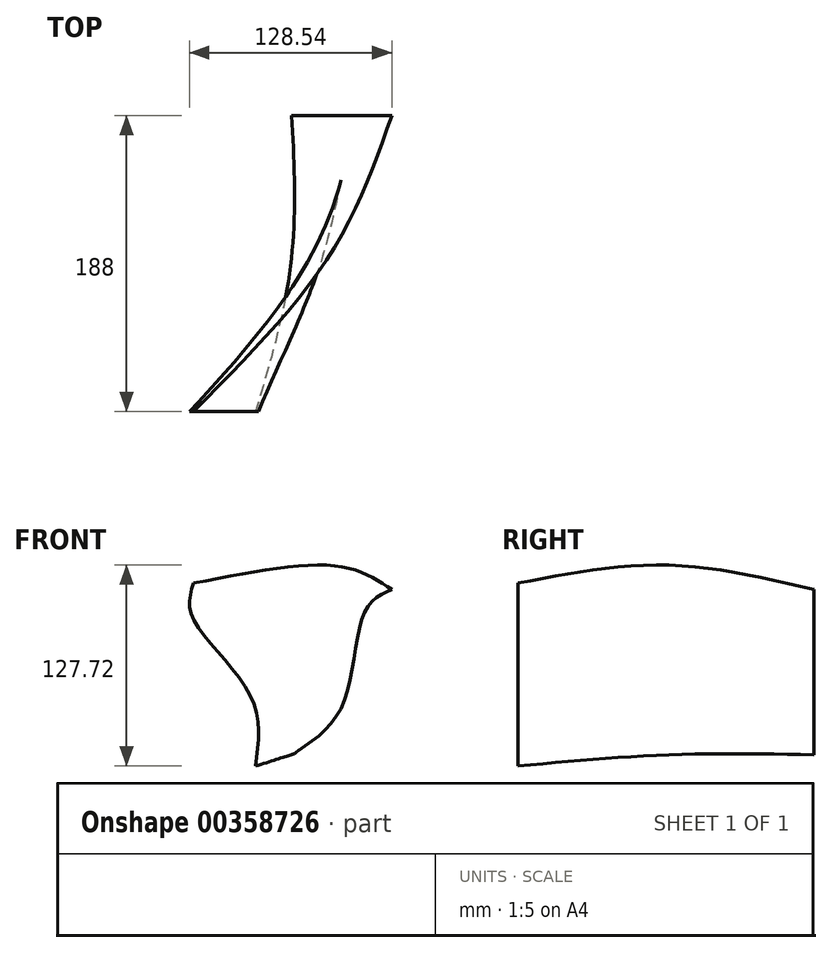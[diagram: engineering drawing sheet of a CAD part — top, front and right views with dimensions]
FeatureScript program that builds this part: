
annotation { "Feature Type Name" : "Feature", "Feature Type Description" : "" }
export const myFeature = defineFeature(function(context is Context, id is Id, definition is map)
    precondition{}
    {
        {
            var Q0;
            Q0=qCreatedBy(makeId("Front.planeOp"),FACE);
            cPlane(context, id + "F0", {"entities" : qUnion([Q0]), "cplaneType" : CPlaneType.OFFSET, "offset" : 115 * mm, "width" : 150 * mm, "height" : 150 * mm});
        }
        {
            var Q0;
            Q0=qCreatedBy(id+"F0.planeOp",FACE);
            cPlane(context, id + "F1", {"entities" : qUnion([Q0]), "cplaneType" : CPlaneType.OFFSET, "offset" : 89 * mm, "width" : 150 * mm, "height" : 150 * mm});
        }
        {
            var Q0;
            Q0=qCreatedBy(id+"F1.planeOp",FACE);
            cPlane(context, id + "F2", {"entities" : qUnion([Q0]), "cplaneType" : CPlaneType.OFFSET, "offset" : 99 * mm, "width" : 150 * mm, "height" : 150 * mm});
        }
        {
            var Q0;
            Q0=qCreatedBy(id+"F2.planeOp",FACE);
            var sketch = newSketch(context, id + "F3", { "sketchPlane" : qUnion([Q0])});
            skFitSpline(sketch, "E0", {"points": [v(-45.29, 49.68) * mm, v(-45.85, 27.84) * mm, v(-9.46, -21.05) * mm, v(-5.86, -66.46) * mm], "startDerivative": vector(-25.44, -84.08) * mm, "endDerivative": vector(-17.12, -129.23) * mm});
            skSolve(sketch);
        }
        {
            var Q0;
            Q0=qCreatedBy(id+"F1.planeOp",FACE);
            var sketch = newSketch(context, id + "F4", { "sketchPlane" : qUnion([Q0])});
            skFitSpline(sketch, "E1", {"points": [v(41.06, 61.05) * mm, v(29.66, 42.42) * mm, v(36.72, -18.12) * mm, v(17.13, -59.24) * mm], "startDerivative": vector(-64.07, -60.1) * mm, "endDerivative": vector(-79.44, -103.35) * mm});
            skSolve(sketch);
        }
        {
            var Q0;
            Q0=qCreatedBy(id+"F0.planeOp",FACE);
            var sketch = newSketch(context, id + "F5", { "sketchPlane" : qUnion([Q0])});
            skFitSpline(sketch, "E2", {"points": [v(80.76, 45.6) * mm, v(63.67, 32) * mm, v(49.6, -27.3) * mm, v(17.13, -59.24) * mm], "startDerivative": vector(-80.76, -34.55) * mm, "endDerivative": vector(-110, -69.95) * mm});
            skSolve(sketch);
        }
        {
            var Q0;
            Q0=sQuery(id+"F5.wireOp",EDGE,"E2");
            var Q1;
            Q1=sQuery(id+"F4.wireOp",EDGE,"E1");
            var Q2;
            Q2=sQuery(id+"F3.wireOp",EDGE,"E0");
            loft(context, id + "F6", {"bodyType" : ToolBodyType.SURFACE, "wireProfilesArray" : [{ "wireProfileEntities" : qUnion([Q0]) }, { "wireProfileEntities" : qUnion([Q1]) }, { "wireProfileEntities" : qUnion([Q2]) }]});
        }
    });
